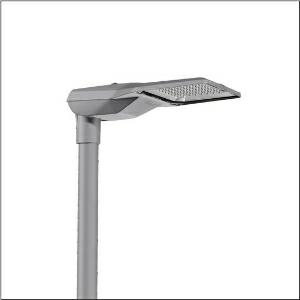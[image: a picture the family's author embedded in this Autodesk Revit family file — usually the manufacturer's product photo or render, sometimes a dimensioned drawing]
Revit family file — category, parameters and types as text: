
# Revit family: streetlight_sl_21_midi___p0_8ab_5xe3r33s08nb_ccbb
name_source: partatom
category: Lighting Fixtures
units: mm (PartAtom-declared; Revit-internal decimal feet)

## family parameters
Cut with Voids When Loaded = No
Host = Face
Light Source = No
Part Type = Normal
Room Calculation Point = No
Round Connector Dimension = Use Diameter
Shared = No

## types (1)
- --- (1 x LED, 19710 lm, 151.2 W, 3000K)
    Apparent Load = 151 VA
    CIE Flux Codes = 39 72 97 100 100
    Color Rendering = 70
    Color Temperature = 3000K
    Default Elevation = 1800 mm
    Description = Streetlight SL 21 midi, mast luminaire, primary light control with lens, of PMMA, primary optical cover: cover, of toughened safety glass, transparent, light distribution: P0.8aB, light emission: direct distribution, primary light characteristic: asymmetric, installation type: post-top, side-entry, LED, High Power LED, rated luminous flux: 19.710lm, luminous efficacy: 130lm/W, light colour: 730, colour temperature: 3000K, control gear: D4i, control: pre-setting: logarithmic dimming characteristic, flexible luminous flux parameterisation, time-dependent luminous flux control, constant luminous flux control, overheat protection, mains connection: 230..240V, AC, 50/60Hz, start of lifetime: 151W, end of service life: 157W, reduction: 70W, luminaire housing, of diecast aluminium, powder-coated, Siteco® metallic grey (DB 702S), corrosivity category C5 mid according to DIN EN ISO 12944, multi-level sealing system, sealing non-destructively replaceable, inclination adjustable: 0°, 5°, 10°, 15°, please order mast flange separately, length: 644mm, width: 335mm, height: 110mm, mast flange for spigot size: 42mm (side-entry): 5XC10008XM4, 60/48mm (side-entry/post-top): 5XC10108XM2, 76/60mm (side-entry/post-top): 5XC10108XM1, mounting height: 4..8m, Smart Interface above, protection rating (complete): IP66, insulation class (complete): insulation class II (safety insulation), certification: CE, ENEC, ENEC+, VDE, impact resistance: IK10, permissible operating ambient temperature for outdoor applications: -40..+50°C, standard-compliant lighting for roads and squares, packaging unit: 1 piece

Light Distribution: P0.8aB
    Height = 111 mm
    Lamp = 1 x LED
    Lamp Light Flux = 19710 lm
    Lamp Power = 151.2 W
    Lamp count = 1
    Length = 644 mm
    Luminous efficacy = 130 lm/W
    Manufacturer = Siteco
    ModVariant = No
    Model = 5XE3R33S08NB
    Number of Poles = 1
    OnlyDefault = Yes
    Power Factor = 1
    Product Name = Streetlight SL 21 midi | P0.8aB
    Product group = mast luminaire | pylon top
    ProductGroupID = 6100
    Protection Class = Protection class II
    Protection Degree = IP 66
    RLX_Detail_Level = 1
    RLX_Emergency_Light_Flux = 0 lm
    RLX_Emergency_Type = 0
    RLX_Emergency_Type_DB = No
    RlxData = <blob elided: 90445 chars, md5=307878cc>
    Socket = socket
    Standby Power = 0 W
    System Light Flux = 19710 lm
    System Power = 151 W
    Type Comments = factory setting: luminous flux: 100 % | dim-lin: 254 | 802 mA
    Type Image = l_1004302.jpg
    URL = http://relux.com
    VarID = @adj_092465
    Voltage = 0 V
    Weight = 0.00 kg
    Width = 336 mm

## geometry (parser evidence)
native form markers: Blend x4, Sweep x11
no freeform markers — native parametric forms only
